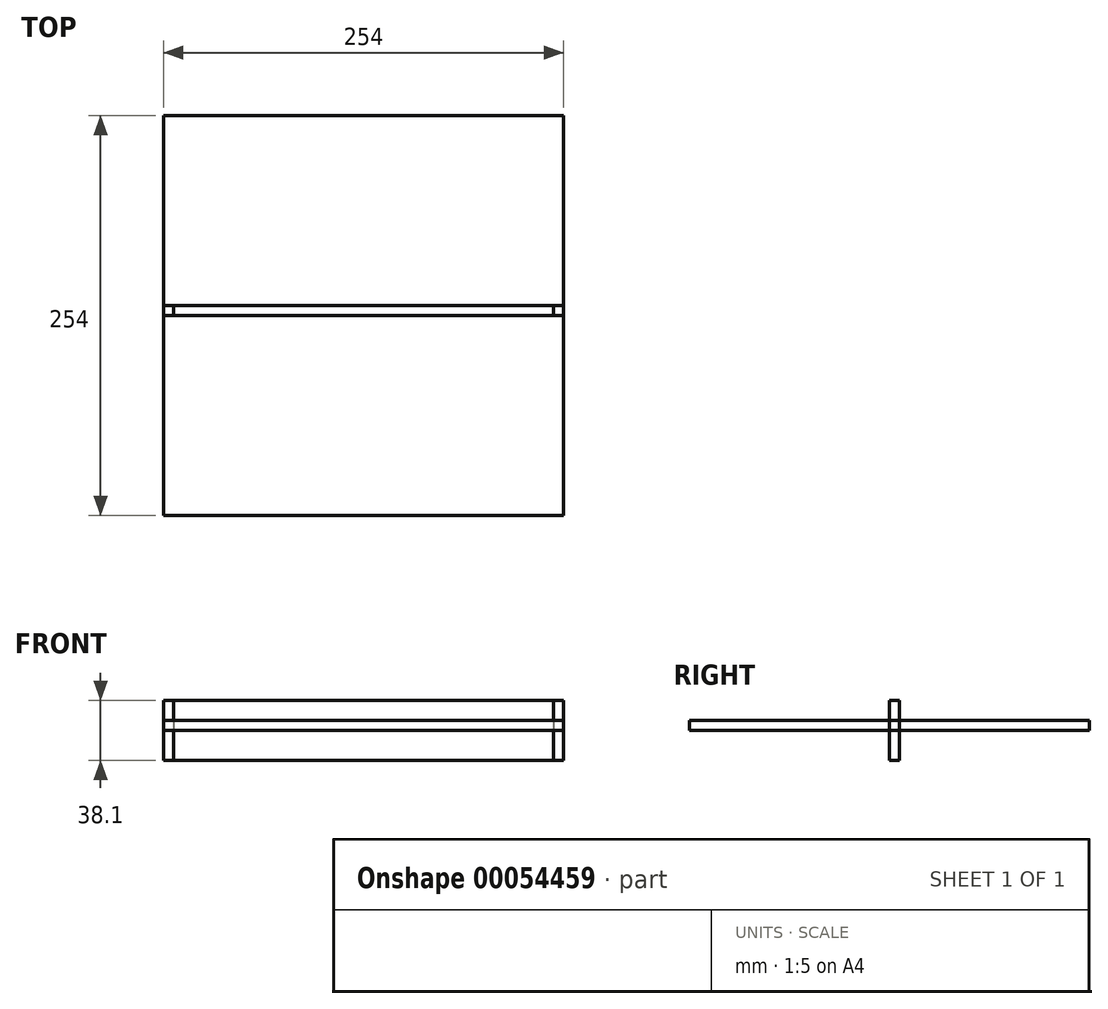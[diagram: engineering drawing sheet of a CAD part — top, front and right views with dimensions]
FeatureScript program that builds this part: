
annotation { "Feature Type Name" : "Feature", "Feature Type Description" : "" }
export const myFeature = defineFeature(function(context is Context, id is Id, definition is map)
    precondition{}
    {
        {
            var Q0;
            Q0=qCreatedBy(makeId("Top.planeOp"),FACE);
            var sketch = newSketch(context, id + "F0", { "sketchPlane" : qUnion([Q0])});
            skLineSegment(sketch, "E0.rect.bottom", {"start": v(127, 127) * mm, "end": v(-127, 127) * mm});
            skLineSegment(sketch, "E0.rect.top", {"start": v(127, -127) * mm, "end": v(-127, -127) * mm});
            skLineSegment(sketch, "E0.rect.left", {"start": v(127, 127) * mm, "end": v(127, -127) * mm});
            skLineSegment(sketch, "E0.rect.right", {"start": v(-127, 127) * mm, "end": v(-127, -127) * mm});
            skPoint(sketch, "E0.rect.middle", {"position": v(0, 0) * mm});
            skSolve(sketch);
        }
        {
            var Q0;
            Q0 = qSketchRegion(id + "F0", true);
            extrude(context, id + "F1", {"entities" : qUnion([Q0]), "depth" : 6.35 * mm});
        }
        {
            var Q0;
            Q0=qCreatedBy(makeId("Front.planeOp"),FACE);
            var sketch = newSketch(context, id + "F2", { "sketchPlane" : qUnion([Q0])});
            skLineSegment(sketch, "E1.rect.bottom", {"start": v(127, 19.05) * mm, "end": v(-127, 19.05) * mm});
            skLineSegment(sketch, "E1.rect.top", {"start": v(127, -19.05) * mm, "end": v(-127, -19.05) * mm});
            skLineSegment(sketch, "E1.rect.left", {"start": v(127, 19.05) * mm, "end": v(127, -19.05) * mm});
            skLineSegment(sketch, "E1.rect.right", {"start": v(-127, 19.05) * mm, "end": v(-127, -19.05) * mm});
            skPoint(sketch, "E1.rect.middle", {"position": v(0, 0) * mm});
            skSolve(sketch);
        }
        {
            var Q0;
            Q0 = qSketchRegion(id + "F2", true);
            extrude(context, id + "F3", {"entities" : qUnion([Q0]), "oppositeDirection" : true, "depth" : 6.35 * mm});
        }
        {
            var Q0;
            Q0=qCreatedBy(makeId("Front.planeOp"),FACE);
            var sketch = newSketch(context, id + "F4", { "sketchPlane" : qUnion([Q0])});
            skLineSegment(sketch, "E2.rect.bottom", {"start": v(120.65, 19.05) * mm, "end": v(-120.65, 19.05) * mm});
            skLineSegment(sketch, "E2.rect.top", {"start": v(120.65, -19.05) * mm, "end": v(-120.65, -19.05) * mm});
            skLineSegment(sketch, "E2.rect.left", {"start": v(120.65, 19.05) * mm, "end": v(120.65, -19.05) * mm});
            skLineSegment(sketch, "E2.rect.right", {"start": v(-120.65, 19.05) * mm, "end": v(-120.65, -19.05) * mm});
            skPoint(sketch, "E2.rect.middle", {"position": v(0, 0) * mm});
            skSolve(sketch);
        }
        {
            var Q0;
            Q0 = qSketchRegion(id + "F4", true);
            extrude(context, id + "F5", {"entities" : qUnion([Q0]), "oppositeDirection" : true, "depth" : 6.35 * mm});
        }
    });
